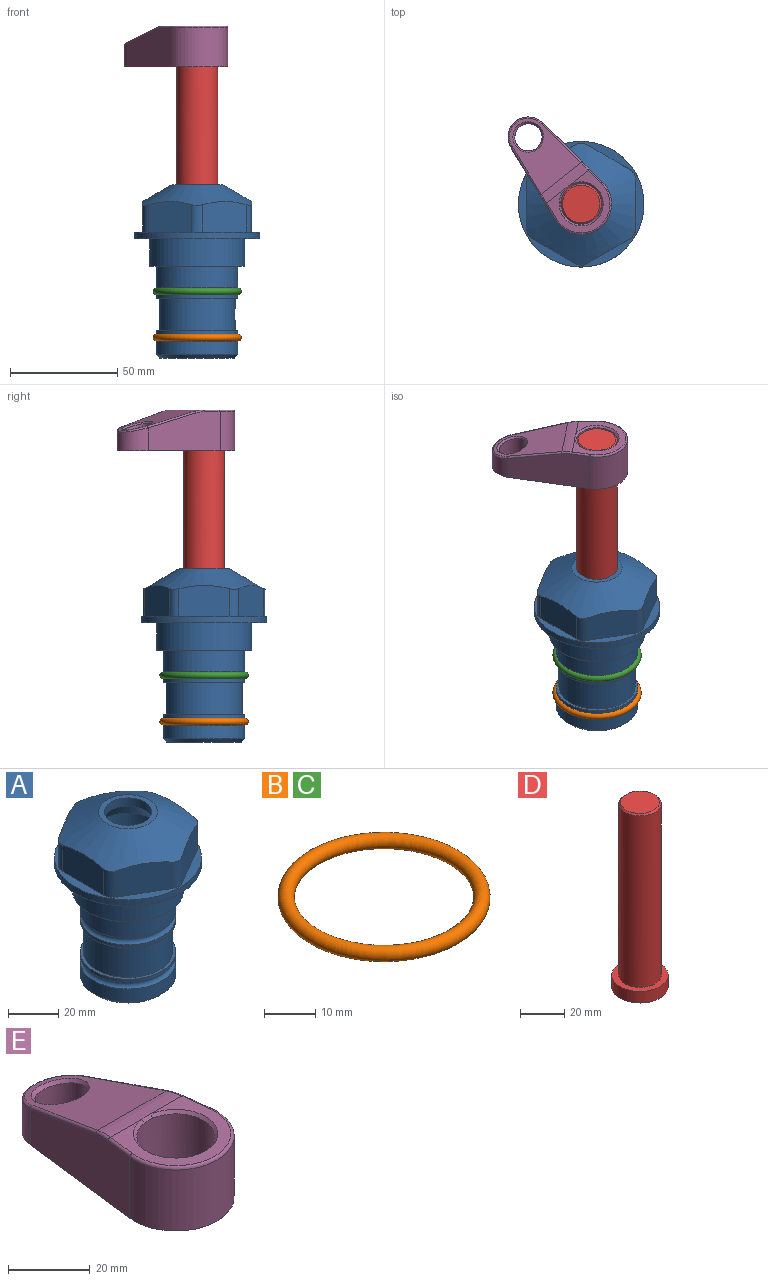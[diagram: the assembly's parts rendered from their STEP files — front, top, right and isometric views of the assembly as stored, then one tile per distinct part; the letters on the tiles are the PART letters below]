
ASSEMBLY  parts=5 mates=4
PART A: 36 faces, bbox 58.7x58.7x81 mm
  f0: cylinder r=17.78mm len=35.56mm, axis (0,0,1), area 1670.8mm2, adj f23,f24,f31
  f1: cylinder r=19.05mm len=38.1mm, axis (0,0,1), area 1191.9mm2, adj f26,f27,f30
  f2: plane 58.66x58.66mm, normal (0,0,-1), area 1150.6mm2, adj f3,f28
  f3: cylinder r=29.33mm len=58.66mm, axis (0,0,-1), area 585.1mm2, adj f2,f4
  f4: plane 58.66x58.66mm, normal (0,0,1), area 475.9mm2, adj f3,f5,f6,f7,f8,f9,f10,f11
  f5: plane 20.32x14.34mm, normal (-0.5,0.87,0), area 324.4mm2, adj f4,f15,f16,f17
  f6: plane 20.32x14.34mm, normal (0.5,0.87,0), area 324.4mm2, adj f4,f14,f15,f17
  f7: plane 23.48x14.34mm, normal (1,0,0), area 324.4mm2, adj f4,f13,f14,f17
  f8: plane 20.32x14.34mm, normal (0.5,-0.87,0), area 324.4mm2, adj f4,f12,f13,f17
  f9: plane 20.32x14.34mm, normal (-0.5,-0.87,0), area 324.4mm2, adj f4,f11,f12,f17
  f10: plane 23.48x14.34mm, normal (-1,0,0), area 324.4mm2, adj f4,f11,f16,f17
  f11: cylinder r=5.08mm len=12.85mm, axis (0,0,-1), area 67.2mm2, adj f4,f9,f10,f17
  f12: cylinder r=5.08mm len=12.85mm, axis (0,0,-1), area 67.2mm2, adj f4,f8,f9,f17
  f13: cylinder r=5.08mm len=12.85mm, axis (0,0,-1), area 67.2mm2, adj f4,f7,f8,f17
  f14: cylinder r=5.08mm len=12.85mm, axis (0,0,-1), area 67.2mm2, adj f4,f6,f7,f17
  f15: cylinder r=5.08mm len=12.85mm, axis (0,0,-1), area 67.2mm2, adj f4,f5,f6,f17
  f16: cylinder r=5.08mm len=12.85mm, axis (0,0,-1), area 67.2mm2, adj f4,f5,f10,f17
  f17: cone r=11.73mm half-angle=60deg, axis (0,0,-1), area 2071.8mm2, adj f5,f6,f7,f8,f9,f10,f11,f12
  f18: plane 23.46x23.46mm, normal (0,0,1), area 147.4mm2, adj f17,f35
  f19: plane 34.93x34.93mm, normal (0,0,-1), area 958mm2, adj f29
  f20: cylinder r=19.05mm len=38.1mm, axis (0,0,1), area 760.1mm2, adj f21,f29
  f21: torus R=19.05mm, axis (0,0,1), area 565.3mm2, adj f20,f22
  f22: cylinder r=19.05mm len=38.1mm, axis (0,0,1), area 190mm2, adj f21,f23
  f23: plane 38.1x38.1mm, normal (0,0,1), area 146.9mm2, adj f0,f22
  f24: plane 38.1x38.1mm, normal (0,0,-1), area 146.9mm2, adj f0,f25
  f25: cylinder r=19.05mm len=38.1mm, axis (0,0,1), area 190mm2, adj f24,f26
  f26: torus R=19.05mm, axis (0,0,1), area 565.3mm2, adj f1,f25
  f27: plane 44.45x44.45mm, normal (0,0,-1), area 411.7mm2, adj f1,f28
  f28: cylinder r=22.23mm len=44.45mm, axis (0,0,1), area 1773.5mm2, adj f2,f27
  f29: cone r=19.05mm half-angle=45deg, axis (0,0,1), area 257.5mm2, adj f19,f20
  f30: cylinder r=3.17mm len=6.75mm, axis (-1,0,0), area 128mm2, adj f1,f33
  f31: cylinder r=3.17mm len=6.35mm, axis (-1,0,0), area 102.5mm2, adj f0,f33
  f32: plane 25.4x25.4mm, normal (0,0,1), area 506.7mm2, adj f33
  f33: cylinder r=12.7mm len=66.42mm, axis (0,0,-1), area 5236.2mm2, adj f30,f31,f32,f34
  f34: cone r=9.53mm half-angle=30deg, axis (0,0,-1), area 443.4mm2, adj f33,f35
  f35: cylinder r=9.53mm len=19.05mm, axis (0,0,-1), area 240.9mm2, adj f18,f34
PART B: 1 faces, bbox 44.7x44.7x3.2 mm
  f0: torus R=19.05mm, axis (0,0,1), area 1193.9mm2
PART C: same geometry as B
PART D: 6 faces, bbox 25.4x25.4x101.6 mm
  f0: plane 17.46x17.46mm, normal (0,0,1), area 239.5mm2, adj f5
  f1: plane 25.4x25.4mm, normal (0,0,-1), area 506.7mm2, adj f2
  f2: cylinder r=12.7mm len=25.4mm, axis (0,0,1), area 506.7mm2, adj f1,f3
  f3: plane 25.4x25.4mm, normal (0,0,1), area 221.7mm2, adj f2,f4
  f4: cylinder r=9.53mm len=94.46mm, axis (0,0,1), area 5653mm2, adj f3,f5
  f5: cone r=8.73mm half-angle=45deg, axis (0,0,-1), area 64.4mm2, adj f0,f4
PART E: 31 faces, bbox 31.7x65.5x19.8 mm
  f0: plane 39.12x18.26mm, normal (0.99,0.12,0), area 612.2mm2, adj f1,f4,f7,f11,f13,f15
  f1: cylinder r=9.53mm len=18.91mm, axis (0,0,-1), area 296.1mm2, adj f0,f2,f7,f17
  f2: plane 39.12x18.26mm, normal (-0.99,0.12,0), area 612.2mm2, adj f1,f4,f7,f12,f14,f16
  f3: cylinder r=6.35mm len=12.7mm, axis (0,0,-1), area 362.4mm2, adj f7,f18
  f4: cylinder r=14.29mm len=28.58mm, axis (0,0,-1), area 882.2mm2, adj f0,f2,f7,f10
  f5: cylinder r=9.53mm len=19.05mm, axis (0,0,-1), area 1092.6mm2, adj f7,f19,f20
  f6: plane 26.99x23.69mm, normal (0,0,1), area 216.2mm2, adj f9,f10,f11,f12,f19
  f7: plane 63.5x28.58mm, normal (0,0,-1), area 661.8mm2, adj f0,f1,f2,f3,f4,f5,f22,f23
  f8: plane 33.52x23.6mm, normal (0,0.26,0.97), area 486mm2, adj f9,f15,f16,f17,f18
  f9: cylinder r=19.05mm len=24.72mm, axis (1,0,0), area 120.4mm2, adj f6,f8,f13,f14,f20
  f10: torus R=13.49mm, axis (0,0,1), area 59mm2, adj f4,f6,f11,f12
  f11: cylinder r=0.79mm len=8.67mm, axis (0.12,-0.99,0), area 10.8mm2, adj f0,f6,f10,f13
  f12: cylinder r=0.79mm len=8.67mm, axis (0.12,0.99,0), area 10.8mm2, adj f2,f6,f10,f14
  f13: bspline ~4.95x1.42mm, area 6.1mm2, adj f0,f9,f11,f15
  f14: bspline ~4.95x1.42mm, area 6.1mm2, adj f2,f9,f12,f16
  f15: cylinder r=0.79mm len=25.95mm, axis (0.12,-0.96,0.26), area 32.9mm2, adj f0,f8,f13,f17
  f16: cylinder r=0.79mm len=25.95mm, axis (0.12,0.96,-0.26), area 32.9mm2, adj f2,f8,f14,f17
  f17: bspline ~18.91x8.38mm, area 30mm2, adj f1,f8,f15,f16
  f18: bspline ~14.29x14.29mm, area 48.3mm2, adj f3,f8
  f19: cone r=9.53mm half-angle=45deg, axis (0,0,1), area 66.5mm2, adj f5,f6,f20
  f20: bspline ~3.22x0.96mm, area 3.5mm2, adj f5,f9,f19
  f21: plane 2.75x2.72mm, normal (0,0,-1), area 2.9mm2, adj f23,f25,f28
  f22: plane 23.05x15.88mm, normal (-0.99,-0.12,0), area 323.6mm2, adj f7,f25,f26,f27,f28,f29
  f23: plane 23.05x15.88mm, normal (0.99,-0.12,0), area 323.6mm2, adj f7,f21,f25,f27,f28,f30
  f24: cylinder r=9.53mm len=10.69mm, axis (0,0,-1), area 114.7mm2, adj f7,f27,f29,f30
  f25: cylinder r=12.7mm len=20.59mm, axis (0,0,-1), area 381.1mm2, adj f7,f21,f22,f23,f26,f28
  f26: plane 2.75x2.72mm, normal (0,0,-1), area 2.9mm2, adj f22,f25,f28
  f27: plane 19.72x18.37mm, normal (0,-0.26,-0.97), area 291.8mm2, adj f22,f23,f24,f28,f29,f30
  f28: cylinder r=15.88mm len=19.92mm, axis (1,0,0), area 54.8mm2, adj f21,f22,f23,f25,f26,f27
  f29: cylinder r=1.59mm len=11mm, axis (0,0,-1), area 34.7mm2, adj f7,f22,f24,f27
  f30: cylinder r=1.59mm len=11mm, axis (0,0,-1), area 34.7mm2, adj f7,f23,f24,f27
PLACE A at identity fixed
PLACE B t=(0,0,-21.59)mm
PLACE C at identity
PLACE D rot(axis=(0,0,1),38.4deg) t=(0,0,35.17)mm
PLACE E rot(axis=(0,0,1),38.4deg) t=(0,0,35.97)mm
MATE fastened E.f4 <-> D.f2  axis (0,0,-1) through (0,0,98.67)mm
MATE fastened B.f0 <-> A.f0  axis (0,0,1) through (0,0,-46.1)mm
MATE cylindrical D.f2 <-> A.f0  axis (0,0,-1) through (0,0,-2.93)mm
MATE fastened C.f0 <-> A.f0  axis (0,0,1) through (0,0,-24.51)mm
